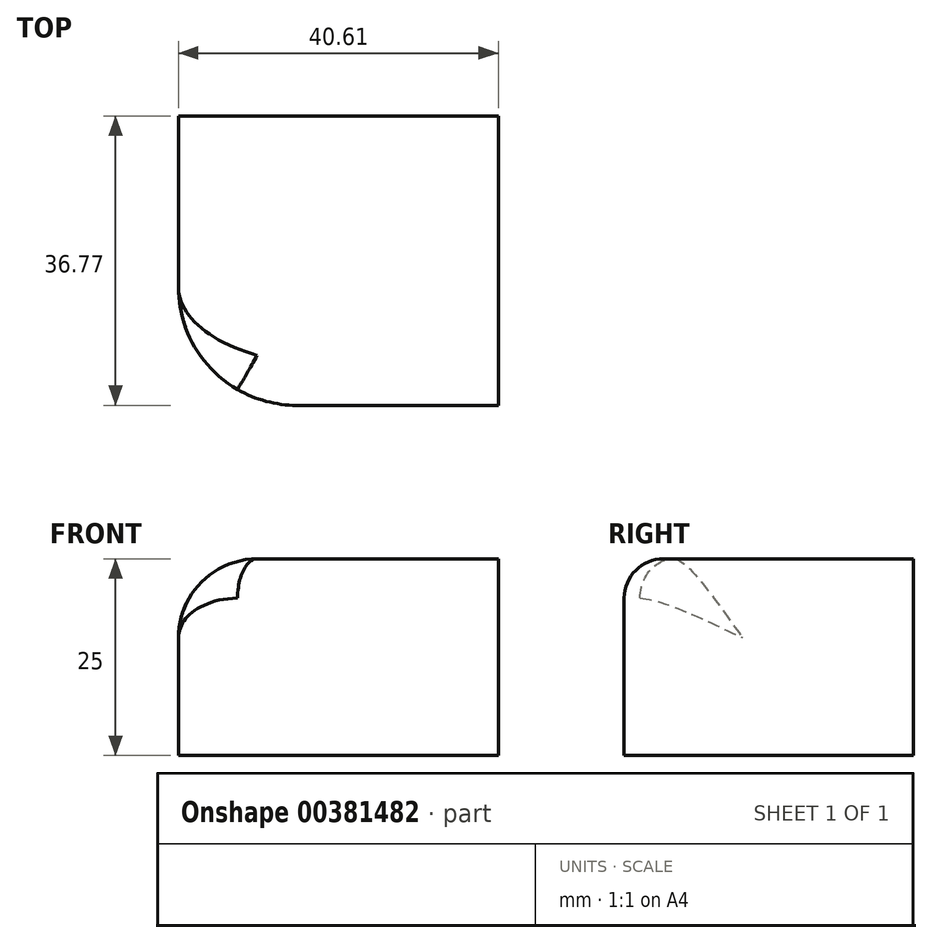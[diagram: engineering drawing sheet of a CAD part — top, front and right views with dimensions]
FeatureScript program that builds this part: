
annotation { "Feature Type Name" : "Feature", "Feature Type Description" : "" }
export const myFeature = defineFeature(function(context is Context, id is Id, definition is map)
    precondition{}
    {
        {
            var Q0;
            Q0=qCreatedBy(makeId("Top.planeOp"),FACE);
            var sketch = newSketch(context, id + "F0", { "sketchPlane" : qUnion([Q0])});
            skLineSegment(sketch, "E0.bottom", {"start": v(0, 0) * mm, "end": v(40.61, 0) * mm});
            skLineSegment(sketch, "E0.top", {"start": v(0, 36.77) * mm, "end": v(40.61, 36.77) * mm});
            skLineSegment(sketch, "E0.left", {"start": v(0, 0) * mm, "end": v(0, 36.77) * mm});
            skLineSegment(sketch, "E0.right", {"start": v(40.61, 0) * mm, "end": v(40.61, 36.77) * mm});
            skSolve(sketch);
        }
        {
            var Q0;
            Q0=makeQuery(id+"F0.imprint","IMPRINT",FACE,{"disambiguationData":[TD([[makeQuery(id+"F0.imprint","IMPRINT",EDGE,{"derivedFrom":sQuery(id+"F0.wireOp",EDGE,"E0.bottom")}),1.0]])]});
            extrude(context, id + "F1", {"entities" : qUnion([Q0]), "depth" : 25 * mm});
        }
        {
            var Q0;
            Q0=makeQuery(id+"F1.opExtrude","CAP_EDGE",EDGE,{"disambiguationData":[OSD([sQuery(id+"F0.wireOp",EDGE,"E0.bottom")])],"isStart":false});
            fillet(context, id + "F2", {"entities" : qUnion([Q0]), "radius" : 5 * mm, "tangentPropagation" : true, "allowEdgeOverflow" : false});
        }
        {
            var Q0;
            Q0=makeQuery(id+"F1.opExtrude","CAP_EDGE",EDGE,{"disambiguationData":[OSD([sQuery(id+"F0.wireOp",EDGE,"E0.left")])],"isStart":false});
            fillet(context, id + "F3", {"entities" : qUnion([Q0]), "radius" : 10 * mm, "allowEdgeOverflow" : false});
        }
        {
            var Q0;
            Q0=makeQuery(id+"F1.opExtrude","SWEPT_EDGE",EDGE,{"disambiguationData":[OSD([sQuery(id+"F0.wireOp",EDGE,"E0.bottom"),sQuery(id+"F0.wireOp",EDGE,"E0.left")])]});
            fillet(context, id + "F4", {"entities" : qUnion([Q0]), "radius" : 15 * mm, "tangentPropagation" : true, "allowEdgeOverflow" : false});
        }
    });
